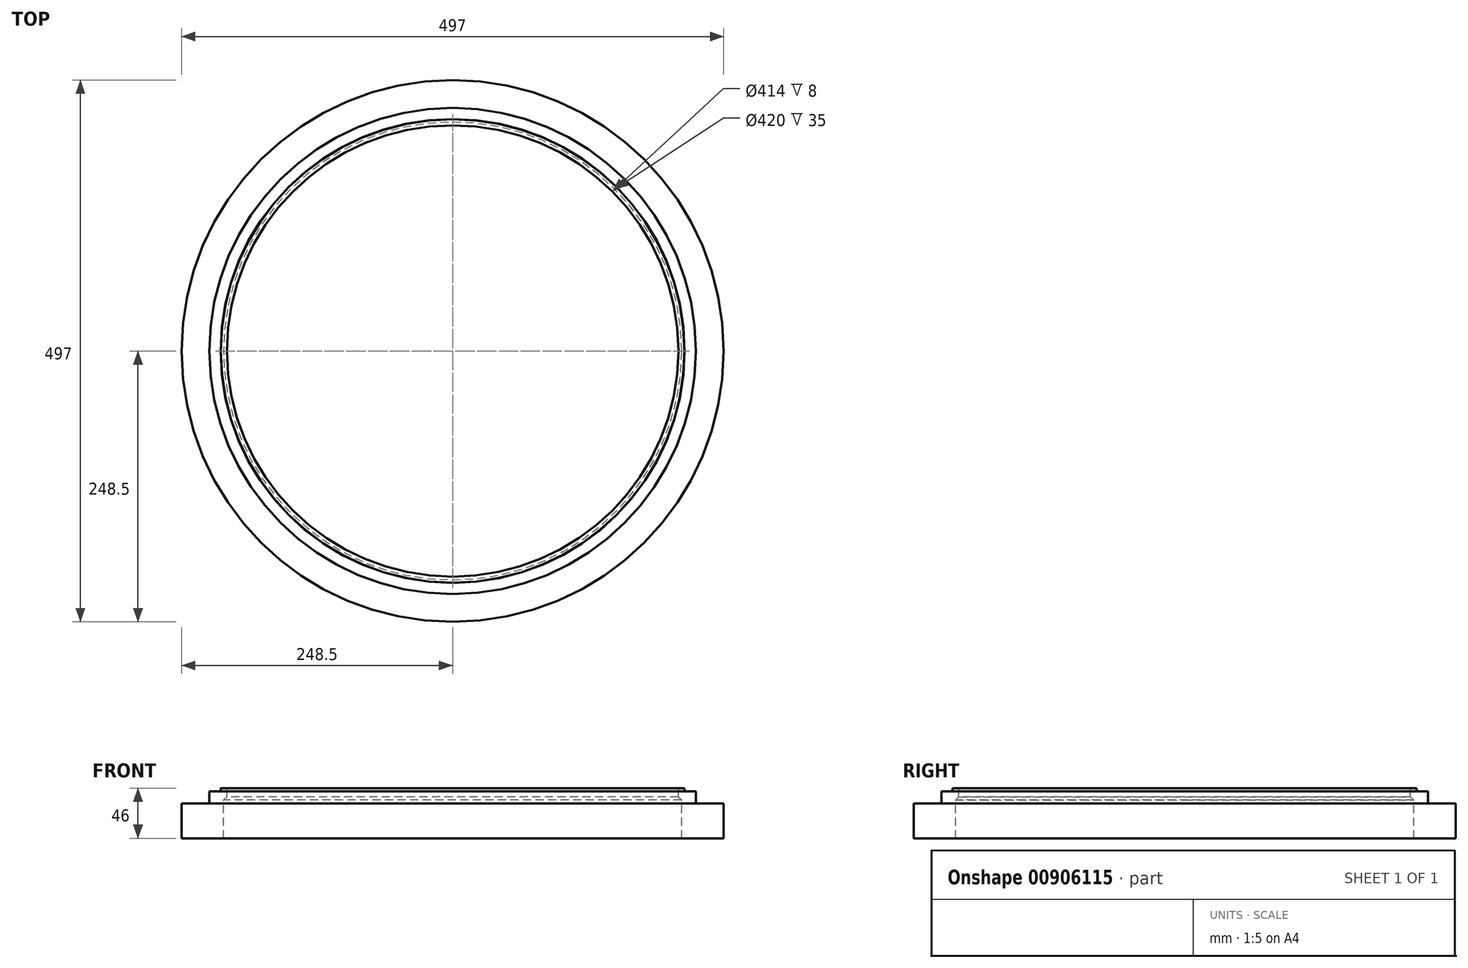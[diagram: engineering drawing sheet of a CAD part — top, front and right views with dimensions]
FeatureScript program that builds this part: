
annotation { "Feature Type Name" : "Feature", "Feature Type Description" : "" }
export const myFeature = defineFeature(function(context is Context, id is Id, definition is map)
    precondition{}
    {
        {
            var Q0;
            Q0=qCreatedBy(makeId("Front.planeOp"),FACE);
            var sketch = newSketch(context, id + "F0", { "sketchPlane" : qUnion([Q0])});
            skLineSegment(sketch, "E0", {"start": v(210, 0) * mm, "end": v(248.5, 0) * mm});
            skLineSegment(sketch, "E1", {"start": v(248.5, 0) * mm, "end": v(248.5, 32) * mm});
            skLineSegment(sketch, "E2", {"start": v(248.5, 32) * mm, "end": v(225, 32) * mm});
            skLineSegment(sketch, "E3", {"start": v(223, 34) * mm, "end": v(223, 43) * mm});
            skLineSegment(sketch, "E4", {"start": v(223, 43) * mm, "end": v(212.7, 43) * mm});
            skLineSegment(sketch, "E5", {"start": v(212.7, 43) * mm, "end": v(212.7, 46) * mm});
            skLineSegment(sketch, "E6", {"start": v(212.7, 46) * mm, "end": v(207, 46) * mm});
            skLineSegment(sketch, "E7", {"start": v(207, 46) * mm, "end": v(207, 38) * mm});
            skLineSegment(sketch, "E8", {"start": v(207, 38) * mm, "end": v(210, 35) * mm});
            skLineSegment(sketch, "E9", {"start": v(210, 35) * mm, "end": v(210, 0) * mm});
            skLineSegment(sketch, "E10", {"start": v(0, 83.16) * mm, "end": v(0, -91.85) * mm, "construction": true});
            skPoint(sketch, "E11.visualSharp", {"position": v(223, 32) * mm});
            skArc(sketch, "E11.filletArc", {"start": v(223, 34) * mm, "mid": v(223.59, 32.59) * mm, "end": v(225, 32) * mm});
            skSolve(sketch);
        }
        {
            var Q0;
            Q0=makeQuery(id+"F0.imprint","IMPRINT",FACE,{"disambiguationData":[TD([[makeQuery(id+"F0.imprint","IMPRINT",EDGE,{"derivedFrom":sQuery(id+"F0.wireOp",EDGE,"E0")}),1.0]])]});
            var Q1;
            Q1=sQuery(id+"F0.wireOp",EDGE,"E10");
            revolve(context, id + "F1", {"surfaceOperationType" : NewSurfaceOperationType.NEW, "entities" : qUnion([Q0]), "axis" : qUnion([Q1]), "revolveType" : RevolveType.FULL});
        }
        {
            var Q0;
            Q0=makeQuery(id+"F1.opRevolve","SWEPT_EDGE",EDGE,{"disambiguationData":[OSD([sQuery(id+"F0.wireOp",EDGE,"E5"),sQuery(id+"F0.wireOp",EDGE,"E6")])]});
            chamfer(context, id + "F2", {"entities" : qUnion([Q0]), "chamferType" : ChamferType.OFFSET_ANGLE, "width" : 0.2 * mm, "oppositeDirection" : false, "angle" : 45 * degree});
        }
    });
